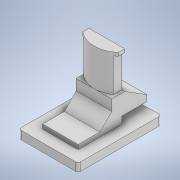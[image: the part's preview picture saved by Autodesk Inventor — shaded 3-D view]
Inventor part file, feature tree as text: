
AUTODESK INVENTOR PART (.ipt)
format: ipt  version: 2021.1 (Build 251245010, 245A)  size: 194,560 bytes
history: native  units: mm
features: sketch x7, extrude x5, fillet x3, other x2, revolve x1
ambient origin geometry x8: Origin, YZ Plane, XZ Plane, XY Plane, X Axis, Y Axis, Z Axis, Center Point
bodies: Body1 (feature_tree)
feature tree (18):
  other  "Твердое тело1"
  extrude  "Выдавливание1"  Depth=15.0mm
  extrude  "Выдавливание2"  Depth=29.0mm
  fillet  "Сопряжение1"  Radius=27.0mm
  fillet  "Сопряжение2"  Radius=25.0mm
  fillet  "Сопряжение3"  Radius=35.0mm
  extrude  "Выдавливание3"  Depth=5.0mm
  extrude  "Выдавливание4"  Depth=5.0mm
  extrude  "Выдавливание5"  Depth=3.5mm TaperAngle=0.0deg
  sketch  "Эскиз7"
  other  "РабПлоскость1"
  revolve  "Вращение2"
  sketch  "Эскиз1"
  sketch  "Эскиз2"
  sketch  "Эскиз3"
  sketch  "Эскиз5"
  sketch  "Эскиз6"
  sketch  "Эскиз8"
